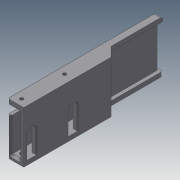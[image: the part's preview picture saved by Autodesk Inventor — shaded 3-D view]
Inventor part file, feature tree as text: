
AUTODESK INVENTOR PART (.ipt)
format: ipt  version: 2020.4 (Build 244396000, 396)  size: 289,280 bytes
history: native  units: in
note: dims shown in document units (in); Inventor stores cm internally (conversion verified against a paired STEP export)
features: chamfer x6, fillet x6, extrude x5, sketch x5, hole x1, mirror x1
ambient origin geometry x8: Origin, YZ Plane, XZ Plane, XY Plane, X Axis, Y Axis, Z Axis, Center Point
bodies: Solid1 (feature_tree)
feature tree (24):
  extrude  "Extrusion1"  Depth=0.25in
  hole  "Hole1"  [1 undecoded]
  extrude  "Extrusion2"  Depth=1.25in
  chamfer  "Chamfer1"  Distance=0.39in
  chamfer  "Chamfer4"  Distance=0.13in
  extrude  "Extrusion4"  Depth=0.425in
  extrude  "Extrusion5"  Depth=0.125in TaperAngle=45.0deg
  fillet  "Fillet2"  Radius=0.5in
  fillet  "Fillet3"  Radius=0.25in
  chamfer  "Chamfer5"  Angle=45.0deg  [1 undecoded]
  chamfer  "Chamfer6"  [1 undecoded]
  fillet  "Fillet4"  Radius=0.5in
  chamfer  "Chamfer7"  Distance=1.5in
  fillet  "Fillet5"  Radius=1.0in
  chamfer  "Chamfer8"  Distance=0.125in
  extrude  "Extrusion6"  Depth=0.125in
  fillet  "Fillet6"  Radius=0.25in
  fillet  "Fillet7"  Radius=0.125in
  mirror  "Mirror1"
  sketch  "Sketch2"  dims[d1=0.25in d2=0.25in]
  sketch  "Sketch3"  dims[d4=0.5in d5=1.625in d6=0.0in]
  sketch  "Sketch5"  dims[d7=1.25in d8=1.25in]
  sketch  "Sketch6"  dims[d9=0.201in d10=0.224in d11=0.375in d12=0.19in d13=0.5635in d14=1.0in d15=0.8108in]
  sketch  "Sketch7"  dims[d16=3.0in d17=0.39in d18=0.13in d19=0.0in d20=0.425in d23=0.125in d24=0.125in d25=45.0deg d33=0.5in d39=0.25in d40=7.0in d41=0.0in d42=0.075in d43=0.125in d44=45.0deg d45=45.0deg d47=0.0in d48=0.0in d49=0.5in d50=1.5in d51=1.0in d52=0.0in d53=0.125in d54=0.125in d55=0.25in d56=0.125in d57=45.0deg d58=0.075in d59=0.125in d60=45.0deg d61=0.125in d62=0.2in d64=5.625in d65=0.125in d66=0.125in d67=45.0deg d68=0.125in d69=0.225in d71=0.05in d72=0.125in d73=45.0deg d74=0.25in d75=0.54in d76=0.85in d77=1.0in d78=0.0in d79=0.26in d80=0.05in]
note: 3 required parameter values undecoded (feature->parameter linkage not recoverable at this tier; creation-order binding heuristic only, values carry confidence <= 0.55)
